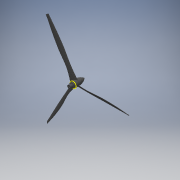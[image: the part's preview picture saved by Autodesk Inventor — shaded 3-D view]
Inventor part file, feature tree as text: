
AUTODESK INVENTOR PART (.ipt)
format: ipt  version: 2018 (Build 220112000, 112)  size: 455,168 bytes
history: native  units: mm
features: sketch x5, plane x3, revolve x1, loft x1, pattern_circular x1
ambient origin geometry x8: Origin, YZ Plane, XZ Plane, XY Plane, X Axis, Y Axis, Z Axis, Center Point
bodies: Solid1 (feature_tree)
feature tree (11):
  revolve  "Revolution1"  [1 undecoded]
  sketch  "Sketch16"  dims[d0=22.5mm d5=26.7mm]
  sketch  "Sketch17"  dims[d6=90.0deg d41=80.0mm d42=130.0mm]
  plane  "Work Plane7"
  sketch  "Sketch18"  dims[d43=190.0mm]
  plane  "Work Plane8"
  sketch  "Sketch19"  dims[d44=0.0mm d45=90.0deg]
  plane  "Work Plane9"
  loft  "Loft3"
  pattern_circular  "Circular Pattern2"  Count=13  [1 undecoded]
  sketch  "Sketch20"  dims[d46=0.0mm d47=90.0deg d48=0.0mm d49=90.0deg d50=0.0mm d51=90.0deg d52=30.0mm d53=360.0deg]
note: 2 required parameter values undecoded (feature->parameter linkage not recoverable at this tier; creation-order binding heuristic only, values carry confidence <= 0.55)